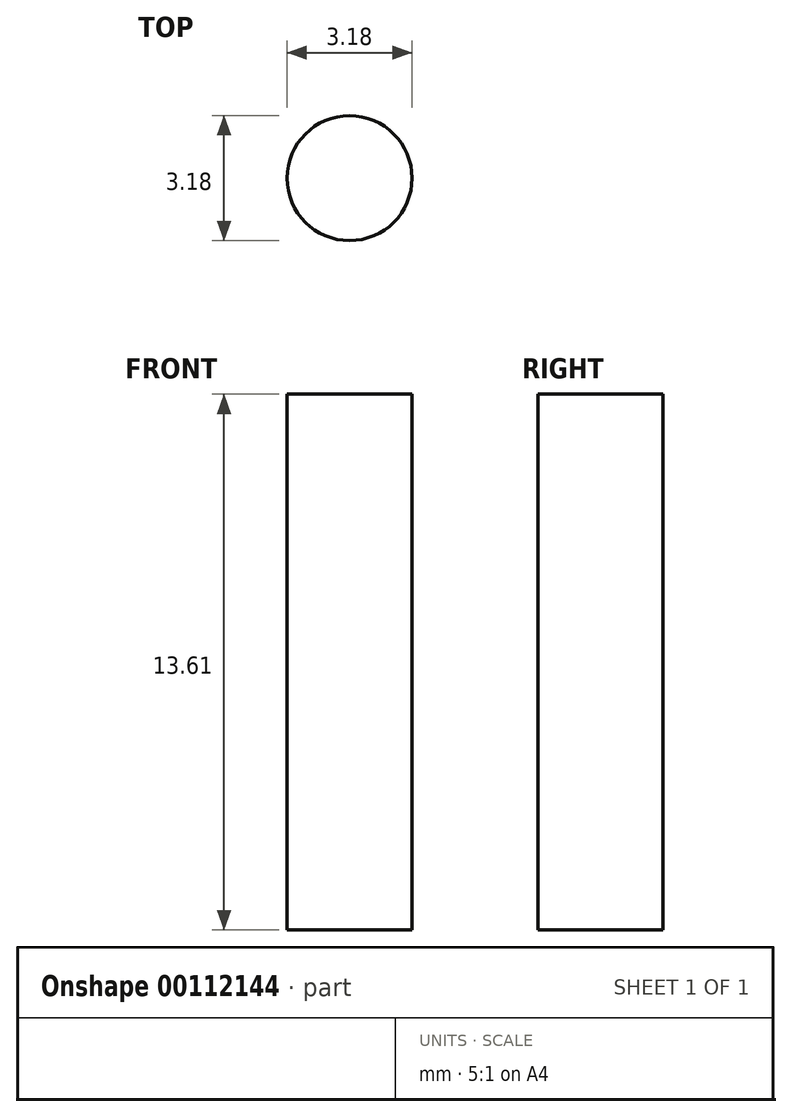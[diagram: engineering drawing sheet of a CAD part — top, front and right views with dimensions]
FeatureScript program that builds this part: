
annotation { "Feature Type Name" : "Feature", "Feature Type Description" : "" }
export const myFeature = defineFeature(function(context is Context, id is Id, definition is map)
    precondition{}
    {
        {
            var Q0;
            Q0=qCreatedBy(makeId("Top.planeOp"),FACE);
            var sketch = newSketch(context, id + "F0", { "sketchPlane" : qUnion([Q0])});
            skCircle(sketch, "E0", {"center": v(0, 0) * mm, "radius": 1.59 * mm});
            skSolve(sketch);
        }
        {
            var Q0;
            Q0=makeQuery(id+"F0.imprint","IMPRINT",FACE,{"disambiguationData":[TD([[makeQuery(id+"F0.imprint","IMPRINT",EDGE,{"derivedFrom":sQuery(id+"F0.wireOp",EDGE,"E0")}),1.0]])]});
            extrude(context, id + "F1", {"entities" : qUnion([Q0]), "depth" : 13.6 * mm});
        }
    });
